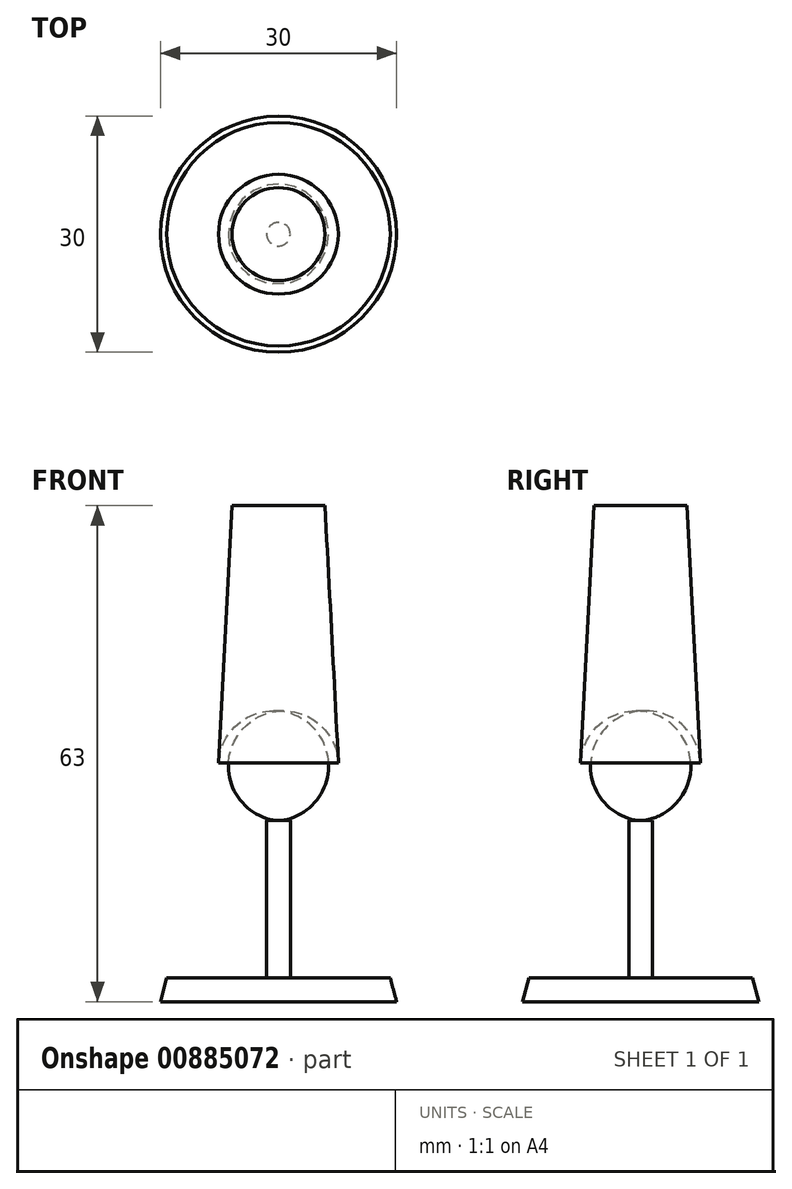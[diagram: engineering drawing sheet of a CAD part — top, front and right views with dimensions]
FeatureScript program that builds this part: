
annotation { "Feature Type Name" : "Feature", "Feature Type Description" : "" }
export const myFeature = defineFeature(function(context is Context, id is Id, definition is map)
    precondition{}
    {
        {
            var Q0;
            Q0=qCreatedBy(makeId("Top.planeOp"),FACE);
            var sketch = newSketch(context, id + "F0", { "sketchPlane" : qUnion([Q0])});
            skCircle(sketch, "E0", {"center": v(0, 0) * mm, "radius": 15 * mm});
            skSolve(sketch);
        }
        {
            var Q0;
            Q0=qSketchRegion(id+"F0",true);
            extrude(context, id + "F1", {"entities" : qUnion([Q0]), "depth" : 3 * mm, "offsetDistance" : 25 * mm, "hasDraft" : true, "draftAngle" : 15 * degree, "draftPullDirection" : true});
        }
        {
            var Q0;
            Q0=makeQuery(id+"F1.opExtrude","CAP_FACE",FACE,{"disambiguationData":[OSD([sQuery(id+"F0.wireOp",EDGE,"E0")])],"isStart":false});
            var sketch = newSketch(context, id + "F2", { "sketchPlane" : qUnion([Q0])});
            skCircle(sketch, "E1", {"center": v(0, 0) * mm, "radius": 1.5 * mm});
            skSolve(sketch);
        }
        {
            var Q0;
            Q0=qSketchRegion(id+"F2",true);
            extrude(context, id + "F3", {"entities" : qUnion([Q0]), "operationType" : NewBodyOperationType.ADD, "depth" : 20 * mm, "offsetDistance" : 25 * mm});
        }
        {
            var Q0;
            Q0=makeQuery(id+"F3.opExtrude","CAP_FACE",FACE,{"disambiguationData":[OSD([sQuery(id+"F2.wireOp",EDGE,"E1")])],"isStart":false});
            var sketch = newSketch(context, id + "F4", { "sketchPlane" : qUnion([Q0])});
            skCircle(sketch, "E2", {"center": v(0, 0) * mm, "radius": 8 * mm});
            skSolve(sketch);
        }
        {
            var Q0;
            Q0=qSketchRegion(id+"F4",true);
            extrude(context, id + "F5", {"entities" : qUnion([Q0]), "operationType" : NewBodyOperationType.ADD, "depth" : 40 * mm, "offsetDistance" : 25 * mm, "hasDraft" : true, "draftAngle" : 3 * degree, "draftPullDirection" : true});
        }
        {
            var Q0;
            Q0=makeQuery(id+"F5.opExtrude","CAP_EDGE",EDGE,{"disambiguationData":[OSD([sQuery(id+"F4.wireOp",EDGE,"E2")])],"isStart":true});
            fillet(context, id + "F6", {"entities" : qUnion([Q0]), "radius" : 7 * mm, "tangentPropagation" : true, "allowEdgeOverflow" : false});
        }
    });
